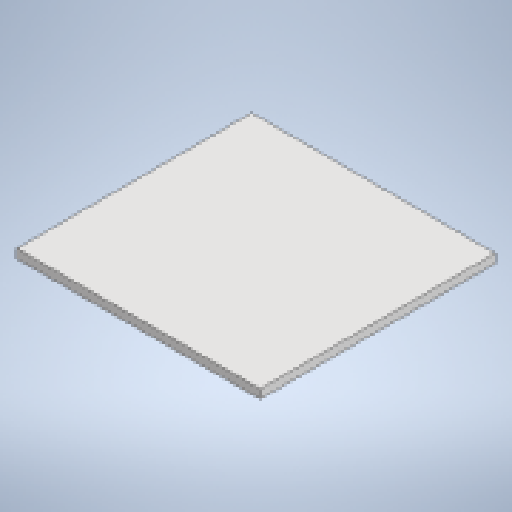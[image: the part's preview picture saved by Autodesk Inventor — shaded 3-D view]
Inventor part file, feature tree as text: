
AUTODESK INVENTOR PART (.ipt)
format: ipt  version: 2024.1 (Build 281209000, 209)  size: 232,960 bytes
history: native  units: mm
features: reference x13, other x4, sketch x3, extrude x2, hole x1
ambient origin geometry x8: Origin, YZ Plane, XZ Plane, XY Plane, X Axis, Y Axis, Z Axis, Center Point
bodies: Solid1 (feature_tree)
feature tree (23):
  extrude  "Extrusion1"  Depth=350.0mm
  extrude  "Extrusion2"  Depth=10.0mm TaperAngle=0.0deg
  hole  "Hole1"  [1 undecoded]
  sketch  "Sketch1"  dims[d0=338.0mm d1=350.0mm]
  sketch  "Sketch2"  dims[d2=12.7mm d3=0.0mm d4=10.0mm d5=0.0mm]
  reference  "Reference1"
  reference  "Reference2"
  reference  "Reference3"
  reference  "Reference4"
  reference  "Reference5"
  reference  "Reference6"
  reference  "Reference7"
  reference  "Reference8"
  reference  "Reference9"
  reference  "Reference10"
  reference  "Reference11"
  reference  "Reference12"
  reference  "Reference13"
  sketch  "Sketch3"  dims[d6=26.211mm d7=60.0mm d8=28.75mm d9=2.0mm d10=90.0deg d11=66.675mm d12=0.0mm]
  other  "<userpath>\OneDrive\Documents\POLEAS\ENSAMBLE BOMBA.iam"
  other  "ENSAMBLE BOMBA.iam"
  other  "WARMAN 4_3:1"
  other  "Part1.1"
note: 1 required parameter value undecoded (feature->parameter linkage not recoverable at this tier; creation-order binding heuristic only, values carry confidence <= 0.55)
